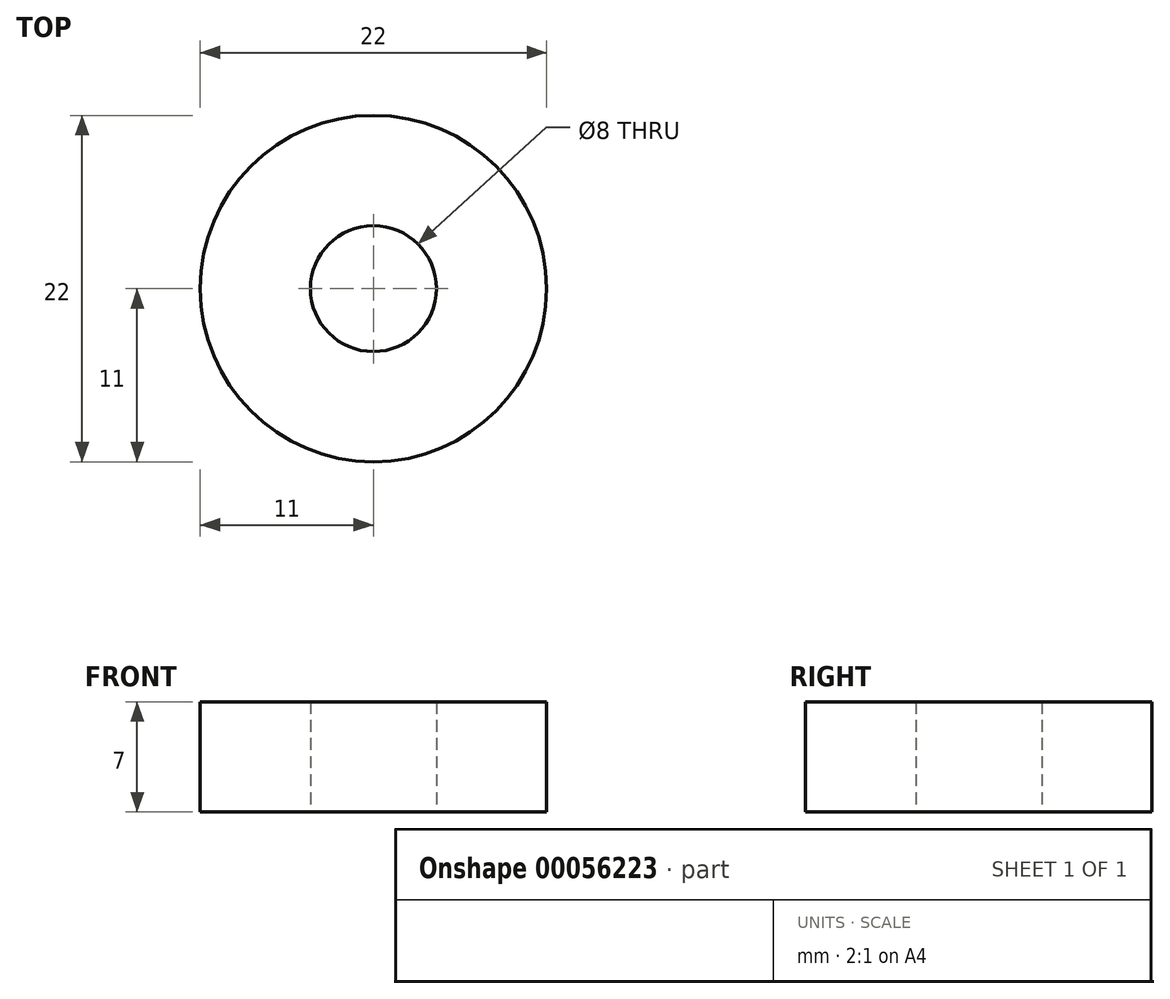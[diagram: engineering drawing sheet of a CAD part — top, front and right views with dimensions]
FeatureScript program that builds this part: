
annotation { "Feature Type Name" : "Feature", "Feature Type Description" : "" }
export const myFeature = defineFeature(function(context is Context, id is Id, definition is map)
    precondition{}
    {
        {
            var Q0;
            Q0=qCreatedBy(makeId("Top.planeOp"),FACE);
            var sketch = newSketch(context, id + "F0", { "sketchPlane" : qUnion([Q0])});
            skCircle(sketch, "E0", {"center": v(0, 0) * mm, "radius": 11 * mm});
            skCircle(sketch, "E1", {"center": v(0, 0) * mm, "radius": 4 * mm});
            skSolve(sketch);
        }
        {
            var Q0;
            Q0=qSketchRegion(id+"F0",true);
            extrude(context, id + "F1", {"entities" : qUnion([Q0]), "depth" : 7 * mm});
        }
    });
